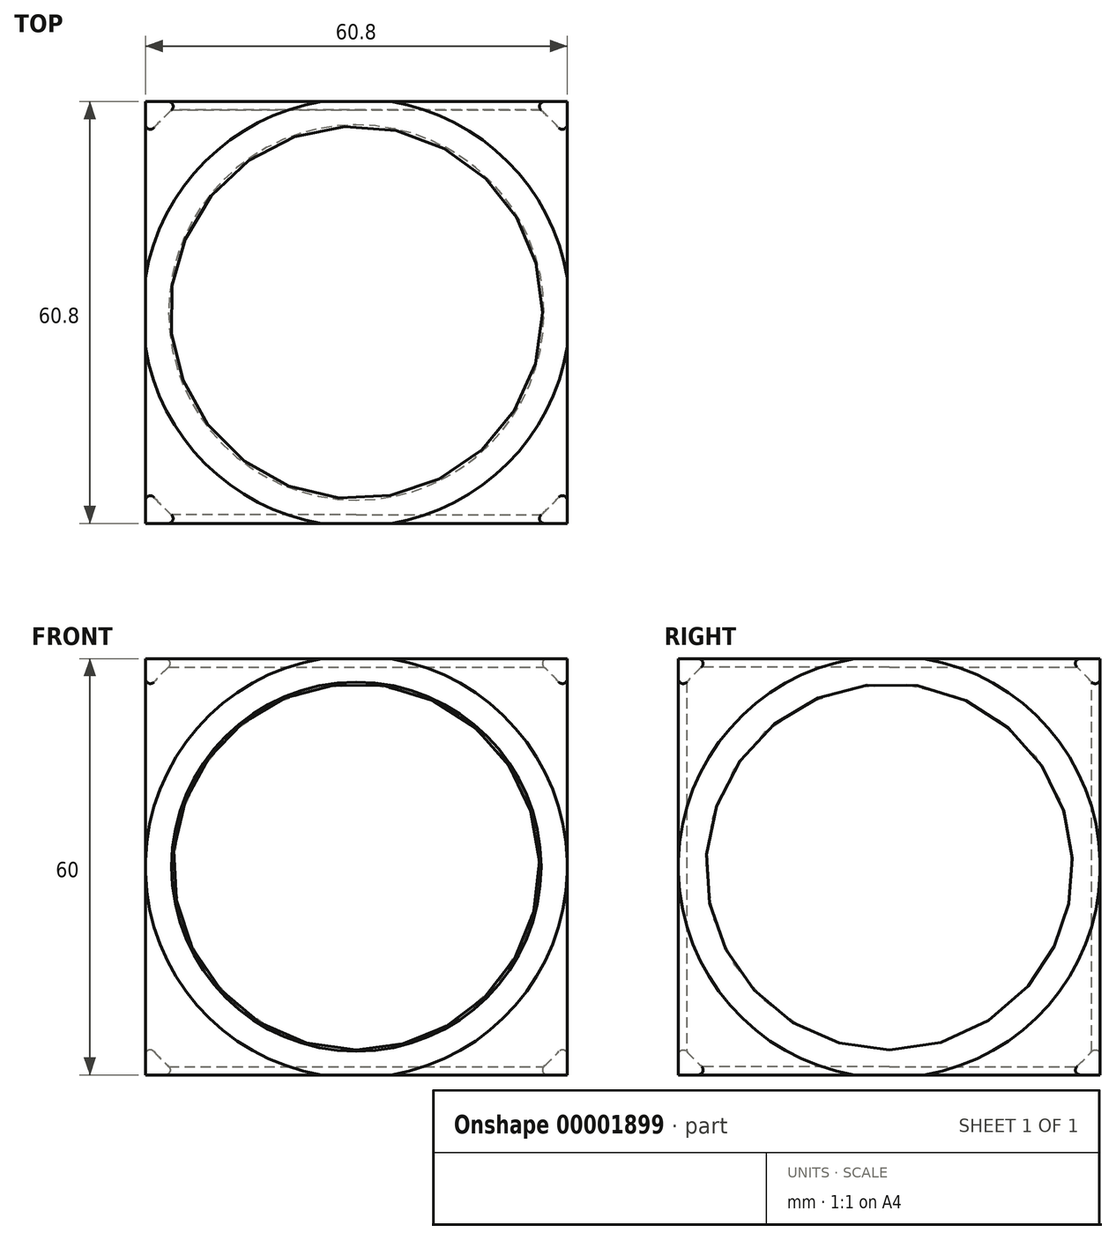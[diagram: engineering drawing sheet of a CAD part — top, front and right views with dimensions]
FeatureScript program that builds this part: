
annotation { "Feature Type Name" : "Feature", "Feature Type Description" : "" }
export const myFeature = defineFeature(function(context is Context, id is Id, definition is map)
    precondition{}
    {
        {
            var Q0;
            Q0=qCreatedBy(makeId("Top.planeOp"),FACE);
            var sketch = newSketch(context, id + "F0", { "sketchPlane" : qUnion([Q0])});
            skLineSegment(sketch, "E0.rect.bottom", {"start": v(25, 25) * mm, "end": v(-25, 25) * mm});
            skLineSegment(sketch, "E0.rect.top", {"start": v(25, -25) * mm, "end": v(-25, -25) * mm});
            skLineSegment(sketch, "E0.rect.left", {"start": v(25, 25) * mm, "end": v(25, -25) * mm});
            skLineSegment(sketch, "E0.rect.right", {"start": v(-25, 25) * mm, "end": v(-25, -25) * mm});
            skPoint(sketch, "E0.rect.middle", {"position": v(0, 0) * mm});
            skSolve(sketch);
        }
        {
            var Q0;
            Q0=qCreatedBy(makeId("Top.planeOp"),FACE);
            var sketch = newSketch(context, id + "F1", { "sketchPlane" : qUnion([Q0])});
            skArc(sketch, "E1", {"start": v(32, 0) * mm, "mid": v(0, 32) * mm, "end": v(-32, 0) * mm});
            skLineSegment(sketch, "E2", {"start": v(-32, 0) * mm, "end": v(32, 0) * mm});
            skSolve(sketch);
        }
        {
            var Q0;
            Q0=qCreatedBy(makeId("Top.planeOp"),FACE);
            var sketch = newSketch(context, id + "F2", { "sketchPlane" : qUnion([Q0])});
            skArc(sketch, "E3.0", {"start": v(34.8, 0) * mm, "mid": v(0, 34.8) * mm, "end": v(-34.8, 0) * mm});
            skArc(sketch, "E4.0", {"start": v(69.8, 0) * mm, "mid": v(0, 69.8) * mm, "end": v(-69.8, 0) * mm});
            skLineSegment(sketch, "E5", {"start": v(-69.8, 0) * mm, "end": v(-34.8, 0) * mm});
            skLineSegment(sketch, "E6", {"start": v(34.8, 0) * mm, "end": v(69.8, 0) * mm});
            skSolve(sketch);
        }
        {
            var Q0;
            Q0=makeQuery(id+"F0.imprint","IMPRINT",FACE,{"disambiguationData":[TD([[makeQuery(id+"F0.imprint","IMPRINT",EDGE,{"derivedFrom":sQuery(id+"F0.wireOp",EDGE,"E0.rect.bottom")}),1.0]])]});
            extrude(context, id + "F3", {"entities" : qUnion([Q0]), "endBound" : BoundingType.SYMMETRIC, "depth" : 50 * mm});
        }
        {
            var Q0;
            Q0=makeQuery(id+"F2.imprint","IMPRINT",FACE,{"disambiguationData":[TD([[makeQuery(id+"F2.imprint","IMPRINT",EDGE,{"derivedFrom":sQuery(id+"F2.wireOp",EDGE,"E3.0")}),-1.0]])]});
            var Q1;
            Q1=sQuery(id+"F2.wireOp",EDGE,"E5");
            revolve(context, id + "F4", {"operationType" : NewBodyOperationType.REMOVE, "entities" : qUnion([Q0]), "axis" : qUnion([Q1]), "revolveType" : RevolveType.FULL, "oppositeDirection" : true});
        }
        {
            var Q0;
            Q0 = qSketchRegion(id + "F1", true);
            var Q1;
            Q1=sQuery(id+"F1.wireOp",EDGE,"E2");
            revolve(context, id + "F5", {"operationType" : NewBodyOperationType.REMOVE, "entities" : qUnion([Q0]), "axis" : qUnion([Q1]), "revolveType" : RevolveType.FULL, "oppositeDirection" : true});
        }
        {
            var Q0;
            Q0=qCreatedBy(makeId("Top.planeOp"),FACE);
            var sketch = newSketch(context, id + "F6", { "sketchPlane" : qUnion([Q0])});
            skArc(sketch, "E7.0", {"start": v(35.4, 0) * mm, "mid": v(0, 35.4) * mm, "end": v(-35.4, 0) * mm});
            skLineSegment(sketch, "E8", {"start": v(-35.4, 0) * mm, "end": v(35.4, 0) * mm});
            skLineSegment(sketch, "E9.rect.bottom", {"start": v(27.7, 27.7) * mm, "end": v(-27.7, 27.7) * mm});
            skLineSegment(sketch, "E9.rect.top", {"start": v(27.7, -27.7) * mm, "end": v(-27.7, -27.7) * mm});
            skLineSegment(sketch, "E9.rect.left", {"start": v(27.7, 27.7) * mm, "end": v(27.7, -27.7) * mm});
            skLineSegment(sketch, "E9.rect.right", {"start": v(-27.7, 27.7) * mm, "end": v(-27.7, -27.7) * mm});
            skArc(sketch, "E10.0", {"start": v(38.9, 0) * mm, "mid": v(0, 38.9) * mm, "end": v(-38.9, 0) * mm});
            skArc(sketch, "E11.0", {"start": v(68.9, 0) * mm, "mid": v(0, 68.9) * mm, "end": v(-68.9, 0) * mm});
            skLineSegment(sketch, "E12", {"start": v(-68.9, 0) * mm, "end": v(-38.9, 0) * mm});
            skLineSegment(sketch, "E13", {"start": v(38.9, 0) * mm, "end": v(68.9, 0) * mm});
            skSolve(sketch);
        }
        {
            var Q0;
            {var subQ1=sQuery(id+"F6.wireOp",EDGE,"E7.0");var subQ3=sQuery(id+"F6.wireOp",EDGE,"E9.rect.bottom");var subQ5=makeQuery(id+"F6.imprint","INTERSECT",VERTEX,{"disambiguationData":[OD(1.0)],"derivedFrom":[subQ1,subQ3]});Q0=makeQuery(id+"F6.imprint","IMPRINT",FACE,{"disambiguationData":[TD([[makeQuery(id+"F6.imprint","IMPRINT",EDGE,{"disambiguationData":[TD([[subQ5,-1.0]])],"derivedFrom":subQ1}),-1.0]])]});}
            var Q1;
            {var subQ3=sQuery(id+"F6.wireOp",EDGE,"E7.0");var subQ5=sQuery(id+"F6.wireOp",EDGE,"E9.rect.left");var subQ7=makeQuery(id+"F6.imprint","INTERSECT",VERTEX,{"derivedFrom":[subQ3,subQ5]});Q1=makeQuery(id+"F6.imprint","IMPRINT",FACE,{"disambiguationData":[TD([[makeQuery(id+"F6.imprint","IMPRINT",EDGE,{"disambiguationData":[TD([[subQ7,-1.0]])],"derivedFrom":subQ3}),1.0]])]});}
            var Q2;
            {var subQ0=sQuery(id+"F6.wireOp",EDGE,"E9.rect.left");var subQ1=sQuery(id+"F6.wireOp",EDGE,"E7.0");var subQ2=makeQuery(id+"F6.imprint","INTERSECT",VERTEX,{"derivedFrom":[subQ1,subQ0]});Q2=makeQuery(id+"F6.imprint","IMPRINT",FACE,{"disambiguationData":[TD([[makeQuery(id+"F6.imprint","IMPRINT",EDGE,{"disambiguationData":[TD([[subQ2,-1.0]])],"derivedFrom":subQ1}),-1.0]])]});}
            var Q3;
            {var subQ3=sQuery(id+"F6.wireOp",EDGE,"E9.rect.top");Q3=makeQuery(id+"F6.imprint","IMPRINT",FACE,{"disambiguationData":[TD([[makeQuery(id+"F6.imprint","IMPRINT",EDGE,{"derivedFrom":subQ3}),-1.0]])]});}
            var Q4;
            {var subQ0=sQuery(id+"F6.wireOp",EDGE,"E9.rect.left");var subQ3=sQuery(id+"F6.wireOp",EDGE,"E9.rect.bottom");var subQ4=makeQuery(id+"F6.imprint","INTERSECT",VERTEX,{"derivedFrom":[subQ3,subQ0]});Q4=makeQuery(id+"F6.imprint","IMPRINT",FACE,{"disambiguationData":[TD([[makeQuery(id+"F6.imprint","IMPRINT",EDGE,{"disambiguationData":[TD([[subQ4,-1.0]])],"derivedFrom":subQ3}),1.0]])]});}
            var Q5;
            {var subQ1=sQuery(id+"F6.wireOp",EDGE,"E9.rect.bottom");var subQ3=sQuery(id+"F6.wireOp",EDGE,"E9.rect.right");var subQ5=makeQuery(id+"F6.imprint","INTERSECT",VERTEX,{"derivedFrom":[subQ1,subQ3]});Q5=makeQuery(id+"F6.imprint","IMPRINT",FACE,{"disambiguationData":[TD([[makeQuery(id+"F6.imprint","IMPRINT",EDGE,{"disambiguationData":[TD([[subQ5,1.0]])],"derivedFrom":subQ1}),1.0]])]});}
            extrude(context, id + "F7", {"entities" : qUnion([Q0, Q1, Q2, Q3, Q4, Q5]), "endBound" : BoundingType.SYMMETRIC, "depth" : 55 * mm});
        }
        {
            var Q0;
            Q0=makeQuery(id+"F6.imprint","IMPRINT",FACE,{"disambiguationData":[TD([[makeQuery(id+"F6.imprint","IMPRINT",EDGE,{"derivedFrom":sQuery(id+"F6.wireOp",EDGE,"E11.0")}),1.0]])]});
            var Q1;
            {var subQ1=sQuery(id+"F6.wireOp",EDGE,"E9.rect.bottom");var subQ3=sQuery(id+"F6.wireOp",EDGE,"E9.rect.right");var subQ5=makeQuery(id+"F6.imprint","INTERSECT",VERTEX,{"derivedFrom":[subQ1,subQ3]});Q1=makeQuery(id+"F6.imprint","IMPRINT",FACE,{"disambiguationData":[TD([[makeQuery(id+"F6.imprint","IMPRINT",EDGE,{"disambiguationData":[TD([[subQ5,1.0]])],"derivedFrom":subQ1}),1.0]])]});}
            var Q2;
            {var subQ0=sQuery(id+"F6.wireOp",EDGE,"E9.rect.left");var subQ3=sQuery(id+"F6.wireOp",EDGE,"E9.rect.bottom");var subQ4=makeQuery(id+"F6.imprint","INTERSECT",VERTEX,{"derivedFrom":[subQ3,subQ0]});Q2=makeQuery(id+"F6.imprint","IMPRINT",FACE,{"disambiguationData":[TD([[makeQuery(id+"F6.imprint","IMPRINT",EDGE,{"disambiguationData":[TD([[subQ4,-1.0]])],"derivedFrom":subQ3}),1.0]])]});}
            var Q3;
            Q3=sQuery(id+"F6.wireOp",EDGE,"E12");
            revolve(context, id + "F8", {"operationType" : NewBodyOperationType.REMOVE, "entities" : qUnion([Q0, Q1, Q2]), "axis" : qUnion([Q3]), "revolveType" : RevolveType.FULL, "oppositeDirection" : true});
        }
        {
            var Q0;
            {var subQ1=sQuery(id+"F6.wireOp",EDGE,"E8");var subQ3=sQuery(id+"F6.wireOp",EDGE,"E7.0");var subQ5=makeQuery(id+"F6.imprint","INTERSECT",VERTEX,{"disambiguationData":[OD(1.0)],"derivedFrom":[subQ3,subQ1]});Q0=makeQuery(id+"F6.imprint","IMPRINT",FACE,{"disambiguationData":[TD([[makeQuery(id+"F6.imprint","IMPRINT",EDGE,{"disambiguationData":[TD([[subQ5,1.0]])],"derivedFrom":subQ3}),1.0]])]});}
            var Q1;
            {var subQ3=sQuery(id+"F6.wireOp",EDGE,"E7.0");var subQ5=sQuery(id+"F6.wireOp",EDGE,"E9.rect.left");var subQ7=makeQuery(id+"F6.imprint","INTERSECT",VERTEX,{"derivedFrom":[subQ3,subQ5]});Q1=makeQuery(id+"F6.imprint","IMPRINT",FACE,{"disambiguationData":[TD([[makeQuery(id+"F6.imprint","IMPRINT",EDGE,{"disambiguationData":[TD([[subQ7,-1.0]])],"derivedFrom":subQ3}),1.0]])]});}
            var Q2;
            {var subQ0=sQuery(id+"F6.wireOp",EDGE,"E9.rect.bottom");var subQ1=sQuery(id+"F6.wireOp",EDGE,"E7.0");var subQ3=makeQuery(id+"F6.imprint","INTERSECT",VERTEX,{"disambiguationData":[OD(0.0)],"derivedFrom":[subQ1,subQ0]});Q2=makeQuery(id+"F6.imprint","IMPRINT",FACE,{"disambiguationData":[TD([[makeQuery(id+"F6.imprint","IMPRINT",EDGE,{"disambiguationData":[TD([[subQ3,-1.0]])],"derivedFrom":subQ1}),1.0]])]});}
            var Q3;
            {var subQ1=sQuery(id+"F6.wireOp",EDGE,"E8");var subQ3=sQuery(id+"F6.wireOp",EDGE,"E7.0");var subQ5=makeQuery(id+"F6.imprint","INTERSECT",VERTEX,{"disambiguationData":[OD(0.0)],"derivedFrom":[subQ3,subQ1]});Q3=makeQuery(id+"F6.imprint","IMPRINT",FACE,{"disambiguationData":[TD([[makeQuery(id+"F6.imprint","IMPRINT",EDGE,{"disambiguationData":[TD([[subQ5,-1.0]])],"derivedFrom":subQ3}),1.0]])]});}
            var Q4;
            Q4=sQuery(id+"F6.wireOp",EDGE,"E8");
            revolve(context, id + "F9", {"operationType" : NewBodyOperationType.REMOVE, "entities" : qUnion([Q0, Q1, Q2, Q3]), "axis" : qUnion([Q4]), "revolveType" : RevolveType.FULL, "oppositeDirection" : true});
        }
        {
            var Q0;
            Q0=qCreatedBy(makeId("Top.planeOp"),FACE);
            var sketch = newSketch(context, id + "F10", { "sketchPlane" : qUnion([Q0])});
            skArc(sketch, "E14.0", {"start": v(39.5, 0) * mm, "mid": v(0, 39.5) * mm, "end": v(-39.5, 0) * mm});
            skLineSegment(sketch, "E15", {"start": v(-39.5, 0) * mm, "end": v(39.5, 0) * mm});
            skLineSegment(sketch, "E16.rect.bottom", {"start": v(30.4, 30.4) * mm, "end": v(-30.4, 30.4) * mm});
            skLineSegment(sketch, "E16.rect.top", {"start": v(30.4, -30.4) * mm, "end": v(-30.4, -30.4) * mm});
            skLineSegment(sketch, "E16.rect.left", {"start": v(30.4, 30.4) * mm, "end": v(30.4, -30.4) * mm});
            skLineSegment(sketch, "E16.rect.right", {"start": v(-30.4, 30.4) * mm, "end": v(-30.4, -30.4) * mm});
            skArc(sketch, "E17.0", {"start": v(43, 0) * mm, "mid": v(0, 43) * mm, "end": v(-43, 0) * mm});
            skArc(sketch, "E18.0", {"start": v(77.92, 0) * mm, "mid": v(0, 77.92) * mm, "end": v(-77.92, 0) * mm});
            skLineSegment(sketch, "E19", {"start": v(-77.92, 0) * mm, "end": v(-43, 0) * mm});
            skLineSegment(sketch, "E20", {"start": v(43, 0) * mm, "end": v(77.92, 0) * mm});
            skSolve(sketch);
        }
        {
            var Q0;
            {var subQ3=sQuery(id+"F10.wireOp",EDGE,"E16.rect.top");Q0=makeQuery(id+"F10.imprint","IMPRINT",FACE,{"disambiguationData":[TD([[makeQuery(id+"F10.imprint","IMPRINT",EDGE,{"derivedFrom":subQ3}),-1.0]])]});}
            var Q1;
            {var subQ3=sQuery(id+"F10.wireOp",EDGE,"E14.0");var subQ8=sQuery(id+"F10.wireOp",EDGE,"E16.rect.left");var subQ10=makeQuery(id+"F10.imprint","INTERSECT",VERTEX,{"derivedFrom":[subQ3,subQ8]});Q1=makeQuery(id+"F10.imprint","IMPRINT",FACE,{"disambiguationData":[TD([[makeQuery(id+"F10.imprint","IMPRINT",EDGE,{"disambiguationData":[TD([[subQ10,-1.0]])],"derivedFrom":subQ3}),1.0]])]});}
            var Q2;
            {var subQ1=sQuery(id+"F10.wireOp",EDGE,"E14.0");var subQ3=sQuery(id+"F10.wireOp",EDGE,"E16.rect.bottom");var subQ5=makeQuery(id+"F10.imprint","INTERSECT",VERTEX,{"disambiguationData":[OD(1.0)],"derivedFrom":[subQ1,subQ3]});Q2=makeQuery(id+"F10.imprint","IMPRINT",FACE,{"disambiguationData":[TD([[makeQuery(id+"F10.imprint","IMPRINT",EDGE,{"disambiguationData":[TD([[subQ5,-1.0]])],"derivedFrom":subQ1}),-1.0]])]});}
            var Q3;
            {var subQ0=sQuery(id+"F10.wireOp",EDGE,"E16.rect.left");var subQ1=sQuery(id+"F10.wireOp",EDGE,"E14.0");var subQ2=makeQuery(id+"F10.imprint","INTERSECT",VERTEX,{"derivedFrom":[subQ1,subQ0]});Q3=makeQuery(id+"F10.imprint","IMPRINT",FACE,{"disambiguationData":[TD([[makeQuery(id+"F10.imprint","IMPRINT",EDGE,{"disambiguationData":[TD([[subQ2,-1.0]])],"derivedFrom":subQ1}),-1.0]])]});}
            var Q4;
            {var subQ1=sQuery(id+"F10.wireOp",EDGE,"E16.rect.bottom");var subQ3=sQuery(id+"F10.wireOp",EDGE,"E16.rect.right");var subQ5=makeQuery(id+"F10.imprint","INTERSECT",VERTEX,{"derivedFrom":[subQ1,subQ3]});Q4=makeQuery(id+"F10.imprint","IMPRINT",FACE,{"disambiguationData":[TD([[makeQuery(id+"F10.imprint","IMPRINT",EDGE,{"disambiguationData":[TD([[subQ5,1.0]])],"derivedFrom":subQ1}),1.0]])]});}
            var Q5;
            {var subQ1=sQuery(id+"F10.wireOp",EDGE,"E16.rect.bottom");var subQ3=sQuery(id+"F10.wireOp",EDGE,"E16.rect.left");var subQ5=makeQuery(id+"F10.imprint","INTERSECT",VERTEX,{"derivedFrom":[subQ1,subQ3]});Q5=makeQuery(id+"F10.imprint","IMPRINT",FACE,{"disambiguationData":[TD([[makeQuery(id+"F10.imprint","IMPRINT",EDGE,{"disambiguationData":[TD([[subQ5,-1.0]])],"derivedFrom":subQ1}),1.0]])]});}
            extrude(context, id + "F11", {"entities" : qUnion([Q0, Q1, Q2, Q3, Q4, Q5]), "endBound" : BoundingType.SYMMETRIC, "depth" : 60 * mm});
        }
        {
            var Q0;
            {var subQ3=sQuery(id+"F10.wireOp",EDGE,"E14.0");var subQ8=sQuery(id+"F10.wireOp",EDGE,"E16.rect.left");var subQ10=makeQuery(id+"F10.imprint","INTERSECT",VERTEX,{"derivedFrom":[subQ3,subQ8]});Q0=makeQuery(id+"F10.imprint","IMPRINT",FACE,{"disambiguationData":[TD([[makeQuery(id+"F10.imprint","IMPRINT",EDGE,{"disambiguationData":[TD([[subQ10,-1.0]])],"derivedFrom":subQ3}),1.0]])]});}
            var Q1;
            {var subQ1=sQuery(id+"F10.wireOp",EDGE,"E15");var subQ3=sQuery(id+"F10.wireOp",EDGE,"E14.0");var subQ5=makeQuery(id+"F10.imprint","INTERSECT",VERTEX,{"disambiguationData":[OD(1.0)],"derivedFrom":[subQ3,subQ1]});Q1=makeQuery(id+"F10.imprint","IMPRINT",FACE,{"disambiguationData":[TD([[makeQuery(id+"F10.imprint","IMPRINT",EDGE,{"disambiguationData":[TD([[subQ5,1.0]])],"derivedFrom":subQ3}),1.0]])]});}
            var Q2;
            {var subQ1=sQuery(id+"F10.wireOp",EDGE,"E15");var subQ3=sQuery(id+"F10.wireOp",EDGE,"E14.0");var subQ5=makeQuery(id+"F10.imprint","INTERSECT",VERTEX,{"disambiguationData":[OD(0.0)],"derivedFrom":[subQ3,subQ1]});Q2=makeQuery(id+"F10.imprint","IMPRINT",FACE,{"disambiguationData":[TD([[makeQuery(id+"F10.imprint","IMPRINT",EDGE,{"disambiguationData":[TD([[subQ5,-1.0]])],"derivedFrom":subQ3}),1.0]])]});}
            var Q3;
            {var subQ0=sQuery(id+"F10.wireOp",EDGE,"E16.rect.bottom");var subQ1=sQuery(id+"F10.wireOp",EDGE,"E14.0");var subQ3=makeQuery(id+"F10.imprint","INTERSECT",VERTEX,{"disambiguationData":[OD(0.0)],"derivedFrom":[subQ1,subQ0]});Q3=makeQuery(id+"F10.imprint","IMPRINT",FACE,{"disambiguationData":[TD([[makeQuery(id+"F10.imprint","IMPRINT",EDGE,{"disambiguationData":[TD([[subQ3,-1.0]])],"derivedFrom":subQ1}),1.0]])]});}
            var Q4;
            Q4=sQuery(id+"F10.wireOp",EDGE,"E15");
            revolve(context, id + "F12", {"operationType" : NewBodyOperationType.REMOVE, "entities" : qUnion([Q0, Q1, Q2, Q3]), "axis" : qUnion([Q4]), "revolveType" : RevolveType.FULL, "oppositeDirection" : true});
        }
        {
            var Q0;
            Q0=makeQuery(id+"F10.imprint","IMPRINT",FACE,{"disambiguationData":[TD([[makeQuery(id+"F10.imprint","IMPRINT",EDGE,{"derivedFrom":sQuery(id+"F10.wireOp",EDGE,"E17.0")}),-1.0]])]});
            var Q1;
            Q1=sQuery(id+"F10.wireOp",EDGE,"E19");
            revolve(context, id + "F13", {"operationType" : NewBodyOperationType.REMOVE, "entities" : qUnion([Q0]), "axis" : qUnion([Q1]), "revolveType" : RevolveType.FULL, "oppositeDirection" : true});
        }
        {
            var Q0;
            Q0=makeQuery(id+"F12.boolean.opBoolean","INTERSECT",EDGE,{"derivedFrom":[makeQuery(id+"F11.opExtrude","CAP_FACE",FACE,{"disambiguationData":[OSD([sQuery(id+"F10.wireOp",EDGE,"E16.rect.bottom"),sQuery(id+"F10.wireOp",EDGE,"E16.rect.top"),sQuery(id+"F10.wireOp",EDGE,"E16.rect.left"),sQuery(id+"F10.wireOp",EDGE,"E16.rect.right")])],"isStart":false}),makeQuery(id+"F12.opRevolve","SWEPT_FACE",FACE,{"disambiguationData":[OSD([sQuery(id+"F10.wireOp",EDGE,"E14.0")])]})]});
            var Q1;
            Q1=makeQuery(id+"F9.boolean.opBoolean","INTERSECT",EDGE,{"derivedFrom":[makeQuery(id+"F7.opExtrude","CAP_FACE",FACE,{"disambiguationData":[OSD([sQuery(id+"F6.wireOp",EDGE,"E9.rect.bottom"),sQuery(id+"F6.wireOp",EDGE,"E9.rect.top"),sQuery(id+"F6.wireOp",EDGE,"E9.rect.left"),sQuery(id+"F6.wireOp",EDGE,"E9.rect.right")])],"isStart":false}),makeQuery(id+"F9.opRevolve","SWEPT_FACE",FACE,{"disambiguationData":[OSD([sQuery(id+"F6.wireOp",EDGE,"E7.0")])]})]});
            var Q2;
            Q2=makeQuery(id+"F12.boolean.opBoolean","INTERSECT",EDGE,{"derivedFrom":[makeQuery(id+"F11.opExtrude","SWEPT_FACE",FACE,{"disambiguationData":[OSD([sQuery(id+"F10.wireOp",EDGE,"E16.rect.top")])]}),makeQuery(id+"F12.opRevolve","SWEPT_FACE",FACE,{"disambiguationData":[OSD([sQuery(id+"F10.wireOp",EDGE,"E14.0")])]})]});
            var Q3;
            Q3=makeQuery(id+"F9.boolean.opBoolean","INTERSECT",EDGE,{"derivedFrom":[makeQuery(id+"F7.opExtrude","SWEPT_FACE",FACE,{"disambiguationData":[OSD([sQuery(id+"F6.wireOp",EDGE,"E9.rect.top")])]}),makeQuery(id+"F9.opRevolve","SWEPT_FACE",FACE,{"disambiguationData":[OSD([sQuery(id+"F6.wireOp",EDGE,"E7.0")])]})]});
            var Q4;
            Q4=makeQuery(id+"F9.boolean.opBoolean","INTERSECT",EDGE,{"derivedFrom":[makeQuery(id+"F7.opExtrude","SWEPT_FACE",FACE,{"disambiguationData":[OSD([sQuery(id+"F6.wireOp",EDGE,"E9.rect.left")])]}),makeQuery(id+"F9.opRevolve","SWEPT_FACE",FACE,{"disambiguationData":[OSD([sQuery(id+"F6.wireOp",EDGE,"E7.0")])]})]});
            var Q5;
            Q5=makeQuery(id+"F12.boolean.opBoolean","INTERSECT",EDGE,{"derivedFrom":[makeQuery(id+"F11.opExtrude","SWEPT_FACE",FACE,{"disambiguationData":[OSD([sQuery(id+"F10.wireOp",EDGE,"E16.rect.left")])]}),makeQuery(id+"F12.opRevolve","SWEPT_FACE",FACE,{"disambiguationData":[OSD([sQuery(id+"F10.wireOp",EDGE,"E14.0")])]})]});
            var Q6;
            Q6=makeQuery(id+"F9.boolean.opBoolean","INTERSECT",EDGE,{"derivedFrom":[makeQuery(id+"F7.opExtrude","SWEPT_FACE",FACE,{"disambiguationData":[OSD([sQuery(id+"F6.wireOp",EDGE,"E9.rect.bottom")])]}),makeQuery(id+"F9.opRevolve","SWEPT_FACE",FACE,{"disambiguationData":[OSD([sQuery(id+"F6.wireOp",EDGE,"E7.0")])]})]});
            var Q7;
            Q7=makeQuery(id+"F12.boolean.opBoolean","INTERSECT",EDGE,{"derivedFrom":[makeQuery(id+"F11.opExtrude","SWEPT_FACE",FACE,{"disambiguationData":[OSD([sQuery(id+"F10.wireOp",EDGE,"E16.rect.bottom")])]}),makeQuery(id+"F12.opRevolve","SWEPT_FACE",FACE,{"disambiguationData":[OSD([sQuery(id+"F10.wireOp",EDGE,"E14.0")])]})]});
            var Q8;
            Q8=makeQuery(id+"F9.boolean.opBoolean","INTERSECT",EDGE,{"derivedFrom":[makeQuery(id+"F7.opExtrude","CAP_FACE",FACE,{"disambiguationData":[OSD([sQuery(id+"F6.wireOp",EDGE,"E9.rect.bottom"),sQuery(id+"F6.wireOp",EDGE,"E9.rect.top"),sQuery(id+"F6.wireOp",EDGE,"E9.rect.left"),sQuery(id+"F6.wireOp",EDGE,"E9.rect.right")])],"isStart":true}),makeQuery(id+"F9.opRevolve","SWEPT_FACE",FACE,{"disambiguationData":[OSD([sQuery(id+"F6.wireOp",EDGE,"E7.0")])]})]});
            var Q9;
            Q9=makeQuery(id+"F12.boolean.opBoolean","INTERSECT",EDGE,{"derivedFrom":[makeQuery(id+"F11.opExtrude","CAP_FACE",FACE,{"disambiguationData":[OSD([sQuery(id+"F10.wireOp",EDGE,"E16.rect.bottom"),sQuery(id+"F10.wireOp",EDGE,"E16.rect.top"),sQuery(id+"F10.wireOp",EDGE,"E16.rect.left"),sQuery(id+"F10.wireOp",EDGE,"E16.rect.right")])],"isStart":true}),makeQuery(id+"F12.opRevolve","SWEPT_FACE",FACE,{"disambiguationData":[OSD([sQuery(id+"F10.wireOp",EDGE,"E14.0")])]})]});
            var Q10;
            Q10=makeQuery(id+"F9.boolean.opBoolean","INTERSECT",EDGE,{"derivedFrom":[makeQuery(id+"F7.opExtrude","SWEPT_FACE",FACE,{"disambiguationData":[OSD([sQuery(id+"F6.wireOp",EDGE,"E9.rect.right")])]}),makeQuery(id+"F9.opRevolve","SWEPT_FACE",FACE,{"disambiguationData":[OSD([sQuery(id+"F6.wireOp",EDGE,"E7.0")])]})]});
            var Q11;
            Q11=makeQuery(id+"F12.boolean.opBoolean","INTERSECT",EDGE,{"derivedFrom":[makeQuery(id+"F11.opExtrude","SWEPT_FACE",FACE,{"disambiguationData":[OSD([sQuery(id+"F10.wireOp",EDGE,"E16.rect.right")])]}),makeQuery(id+"F12.opRevolve","SWEPT_FACE",FACE,{"disambiguationData":[OSD([sQuery(id+"F10.wireOp",EDGE,"E14.0")])]})]});
            var Q12;
            Q12=makeQuery(id+"F5.boolean.opBoolean","INTERSECT",EDGE,{"derivedFrom":[makeQuery(id+"F3.opExtrude","SWEPT_FACE",FACE,{"disambiguationData":[OSD([sQuery(id+"F0.wireOp",EDGE,"E0.rect.bottom")])]}),makeQuery(id+"F5.opRevolve","SWEPT_FACE",FACE,{"disambiguationData":[OSD([sQuery(id+"F1.wireOp",EDGE,"E1")])]})]});
            var Q13;
            Q13=makeQuery(id+"F5.boolean.opBoolean","INTERSECT",EDGE,{"derivedFrom":[makeQuery(id+"F3.opExtrude","SWEPT_FACE",FACE,{"disambiguationData":[OSD([sQuery(id+"F0.wireOp",EDGE,"E0.rect.right")])]}),makeQuery(id+"F5.opRevolve","SWEPT_FACE",FACE,{"disambiguationData":[OSD([sQuery(id+"F1.wireOp",EDGE,"E1")])]})]});
            var Q14;
            Q14=makeQuery(id+"F5.boolean.opBoolean","INTERSECT",EDGE,{"derivedFrom":[makeQuery(id+"F3.opExtrude","CAP_FACE",FACE,{"disambiguationData":[OSD([sQuery(id+"F0.wireOp",EDGE,"E0.rect.bottom"),sQuery(id+"F0.wireOp",EDGE,"E0.rect.top"),sQuery(id+"F0.wireOp",EDGE,"E0.rect.left"),sQuery(id+"F0.wireOp",EDGE,"E0.rect.right")])],"isStart":false}),makeQuery(id+"F5.opRevolve","SWEPT_FACE",FACE,{"disambiguationData":[OSD([sQuery(id+"F1.wireOp",EDGE,"E1")])]})]});
            var Q15;
            Q15=makeQuery(id+"F5.boolean.opBoolean","INTERSECT",EDGE,{"derivedFrom":[makeQuery(id+"F3.opExtrude","SWEPT_FACE",FACE,{"disambiguationData":[OSD([sQuery(id+"F0.wireOp",EDGE,"E0.rect.left")])]}),makeQuery(id+"F5.opRevolve","SWEPT_FACE",FACE,{"disambiguationData":[OSD([sQuery(id+"F1.wireOp",EDGE,"E1")])]})]});
            var Q16;
            Q16=makeQuery(id+"F5.boolean.opBoolean","INTERSECT",EDGE,{"derivedFrom":[makeQuery(id+"F3.opExtrude","CAP_FACE",FACE,{"disambiguationData":[OSD([sQuery(id+"F0.wireOp",EDGE,"E0.rect.bottom"),sQuery(id+"F0.wireOp",EDGE,"E0.rect.top"),sQuery(id+"F0.wireOp",EDGE,"E0.rect.left"),sQuery(id+"F0.wireOp",EDGE,"E0.rect.right")])],"isStart":true}),makeQuery(id+"F5.opRevolve","SWEPT_FACE",FACE,{"disambiguationData":[OSD([sQuery(id+"F1.wireOp",EDGE,"E1")])]})]});
            var Q17;
            Q17=makeQuery(id+"F5.boolean.opBoolean","INTERSECT",EDGE,{"derivedFrom":[makeQuery(id+"F3.opExtrude","SWEPT_FACE",FACE,{"disambiguationData":[OSD([sQuery(id+"F0.wireOp",EDGE,"E0.rect.top")])]}),makeQuery(id+"F5.opRevolve","SWEPT_FACE",FACE,{"disambiguationData":[OSD([sQuery(id+"F1.wireOp",EDGE,"E1")])]})]});
            fillet(context, id + "F14", {"entities" : qUnion([Q0, Q1, Q2, Q3, Q4, Q5, Q6, Q7, Q8, Q9, Q10, Q11, Q12, Q13, Q14, Q15, Q16, Q17]), "radius" : .7 * mm, "tangentPropagation" : true, "allowEdgeOverflow" : false});
        }
    });
